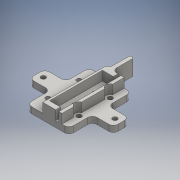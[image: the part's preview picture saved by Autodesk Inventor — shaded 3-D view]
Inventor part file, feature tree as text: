
AUTODESK INVENTOR PART (.ipt)
format: ipt  version: 2016 SP1 (Build 200210100, 210)  size: 370,176 bytes
history: native  units: mm
features: extrude x10, sketch x8, fillet x5, projected_geometry x2, hole x1
ambient origin geometry x8: Origin, YZ Plane, XZ Plane, XY Plane, X Axis, Y Axis, Z Axis, Center Point
bodies: Solid1 (feature_tree)
feature tree (26):
  extrude  "Extrusion1"  Depth=3.0mm
  extrude  "Extrusion2"  Depth=10.0mm
  extrude  "Extrusion3"  Depth=3.0mm
  extrude  "Extrusion4"  Depth=20.0mm
  extrude  "Extrusion5"  Depth=10.0mm
  hole  "Hole1"  [1 undecoded]
  fillet  "Fillet5"  Radius=40.0mm
  fillet  "Fillet7"  Radius=10.0mm
  extrude  "Extrusion7"  Depth=4.0mm
  fillet  "Fillet9"  Radius=6.0mm
  extrude  "Extrusion8"  Depth=1.0mm
  extrude  "Extrusion10"  Depth=15.0mm
  fillet  "Fillet10"  Radius=2.0mm
  fillet  "Fillet11"  Radius=2.0mm
  extrude  "Extrusion9"  Depth=12.0mm
  extrude  "Extrusion6"  Depth=1.0mm
  sketch  "Sketch3"  dims[d0=3.0mm d1=3.0mm]
  sketch  "Sketch4"  dims[d2=20.0mm d3=10.0mm]
  sketch  "Sketch5"  dims[d4=3.0mm d5=3.0mm]
  sketch  "Sketch9"  dims[d6=20.0mm d7=20.0mm]
  sketch  "Sketch11"  dims[d8=20.0mm d9=10.0mm]
  sketch  "Sketch12"  dims[d10=30.0mm d11=15.0mm d12=40.0mm d13=10.0mm]
  projected_geometry  "Projected Loop2"
  sketch  "Sketch13"  dims[d14=4.0mm d15=0.0mm d16=4.0mm d20=6.0mm d21=0.0mm]
  projected_geometry  "Projected Loop3"
  sketch  "Sketch14"  dims[d23=2.5mm d24=2.5mm d25=15.0mm d26=2.0mm d27=2.0mm d28=12.0mm d29=2.5mm d30=6.0mm d31=4.0mm d32=2.0mm d33=90.0deg d34=8.0mm d35=20.594885mm d36=6.3mm d37=5.5mm d38=5.5mm d39=8.0mm d40=0.0mm d47=8.0mm d48=0.0mm d77=10.0mm d78=40.0mm d79=15.0mm d80=3.0mm d81=3.0mm d82=46.0mm d83=54.0mm d84=23.0mm d85=27.0mm d86=8.0mm d87=0.0mm d90=8.0mm d91=0.0mm d94=1.0mm d96=0.0mm d97=0.0mm d110=2.0mm d111=0.7mm d112=3.0mm d115=3.0mm d116=1.3mm d117=2.0mm d118=2.0mm d119=2.0mm d121=27.0mm d122=13.5mm d123=10.0mm d124=0.0mm d125=3.0mm d126=3.0mm d128=6.0mm d129=3.0mm d130=10.0mm d131=0.0mm d132=3.0mm d133=21.0mm d134=4.0mm d135=2.0mm d136=10.5mm d137=10.0mm d138=0.0mm d139=0.0mm d140=0.0mm d141=22.0mm d142=14.0mm d143=1.2mm d144=1.2mm d145=10.0mm d146=0.0mm d147=3.0mm d148=1.0mm]
note: 1 required parameter value undecoded (feature->parameter linkage not recoverable at this tier; creation-order binding heuristic only, values carry confidence <= 0.55)
